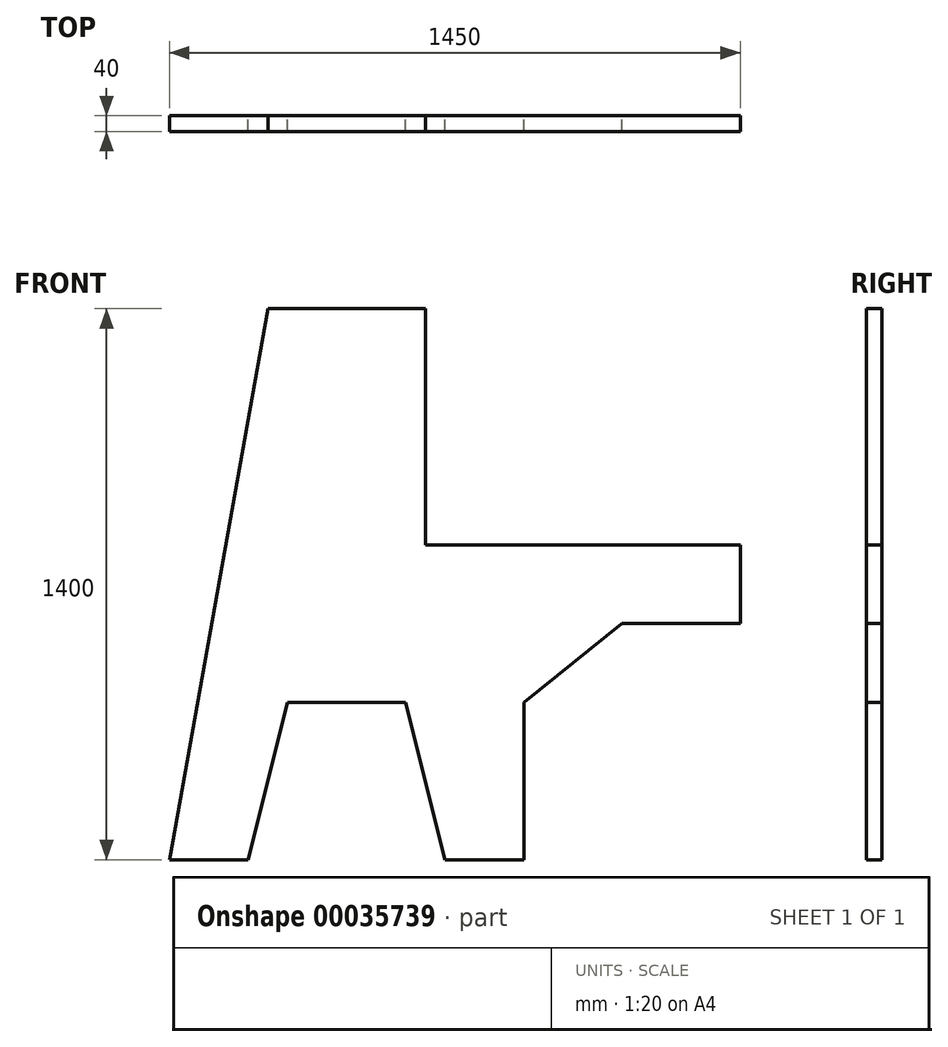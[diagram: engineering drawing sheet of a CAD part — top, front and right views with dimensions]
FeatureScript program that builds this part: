
annotation { "Feature Type Name" : "Feature", "Feature Type Description" : "" }
export const myFeature = defineFeature(function(context is Context, id is Id, definition is map)
    precondition{}
    {
        {
            var Q0;
            Q0=qCreatedBy(makeId("Front.planeOp"),FACE);
            var sketch = newSketch(context, id + "F0", { "sketchPlane" : qUnion([Q0])});
            skLineSegment(sketch, "E0", {"start": v(0, 291.3) * mm, "end": v(400, 291.3) * mm});
            skLineSegment(sketch, "E1", {"start": v(400, 291.3) * mm, "end": v(400, -308.7) * mm});
            skLineSegment(sketch, "E2", {"start": v(400, -308.7) * mm, "end": v(1200, -308.7) * mm});
            skLineSegment(sketch, "E3", {"start": v(1200, -308.7) * mm, "end": v(1200, -508.7) * mm});
            skLineSegment(sketch, "E4", {"start": v(1200, -508.7) * mm, "end": v(900, -508.7) * mm});
            skLineSegment(sketch, "E5", {"start": v(450, -1108.7) * mm, "end": v(650, -1108.7) * mm});
            skLineSegment(sketch, "E6", {"start": v(-50, -1108.7) * mm, "end": v(-250, -1108.7) * mm});
            skLineSegment(sketch, "E7", {"start": v(650, -1108.7) * mm, "end": v(650, -708.7) * mm});
            skLineSegment(sketch, "E8", {"start": v(650, -708.7) * mm, "end": v(900, -508.7) * mm});
            skLineSegment(sketch, "E9", {"start": v(0, 291.3) * mm, "end": v(-250, -1108.7) * mm});
            skLineSegment(sketch, "E10", {"start": v(200, -708.7) * mm, "end": v(50, -708.7) * mm});
            skLineSegment(sketch, "E11", {"start": v(-50, -1108.7) * mm, "end": v(50, -708.7) * mm});
            skLineSegment(sketch, "E12", {"start": v(200, -708.7) * mm, "end": v(350, -708.7) * mm});
            skLineSegment(sketch, "E13", {"start": v(350, -708.7) * mm, "end": v(450, -1108.7) * mm});
            skPoint(sketch, "E14.orphan", {"position": v(0, -708.7) * mm});
            skPoint(sketch, "E15.orphan", {"position": v(200, 291.3) * mm});
            skSolve(sketch);
        }
        {
            var Q0;
            Q0 = qSketchRegion(id + "F0", true);
            extrude(context, id + "F1", {"entities" : qUnion([Q0]), "depth" : 40 * mm});
        }
    });
